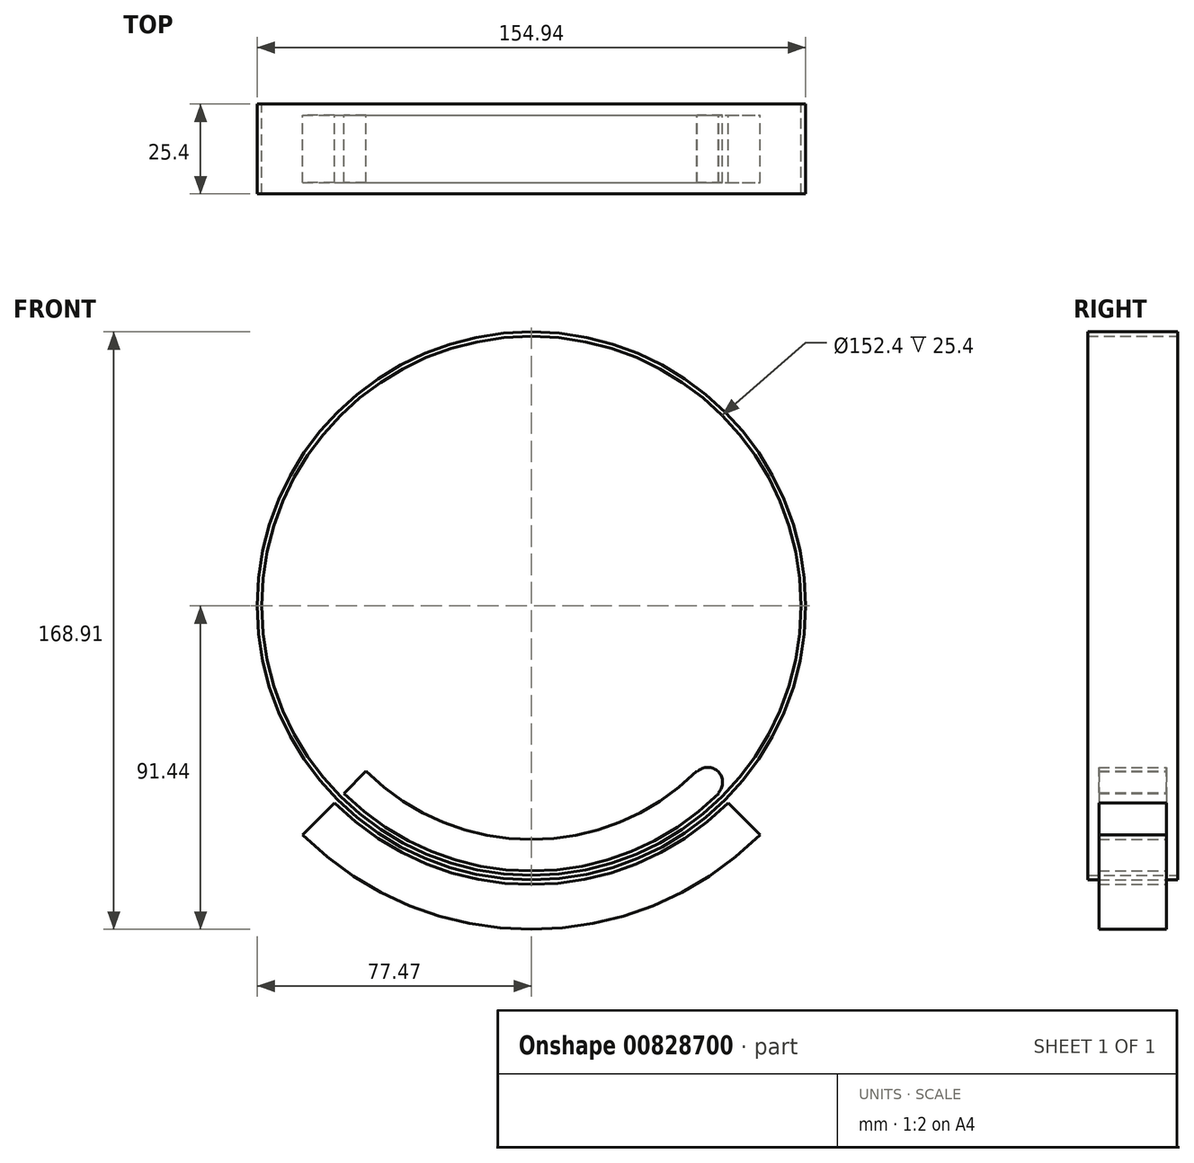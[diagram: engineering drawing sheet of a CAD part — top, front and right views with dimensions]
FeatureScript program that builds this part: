
annotation { "Feature Type Name" : "Feature", "Feature Type Description" : "" }
export const myFeature = defineFeature(function(context is Context, id is Id, definition is map)
    precondition{}
    {
        {
            var Q0;
            Q0=qCreatedBy(makeId("Front.planeOp"),FACE);
            var sketch = newSketch(context, id + "F0", { "sketchPlane" : qUnion([Q0])});
            skCircle(sketch, "E0", {"center": v(0, 0) * mm, "radius": 76.2 * mm});
            skCircle(sketch, "E1", {"center": v(0, 0) * mm, "radius": 77.47 * mm});
            skSolve(sketch);
        }
        {
            var Q0;
            Q0=qSketchRegion(id+"F0",true);
            extrude(context, id + "F1", {"entities" : qUnion([Q0]), "depth" : 25.4 * mm, "offsetDistance" : 25.4 * mm, "symmetric" : true});
        }
        {
            var Q0;
            Q0=qCreatedBy(makeId("Front.planeOp"),FACE);
            var sketch = newSketch(context, id + "F2", { "sketchPlane" : qUnion([Q0])});
            skLineSegment(sketch, "E2", {"start": v(-46.7, -46.7) * mm, "end": v(-52.98, -52.98) * mm});
            skLineSegment(sketch, "E3", {"start": v(46.7, -46.7) * mm, "end": v(46.88, -46.88) * mm});
            skArc(sketch, "E4", {"start": v(-52.98, -52.98) * mm, "mid": v(0, -74.93) * mm, "end": v(52.98, -52.98) * mm});
            skArc(sketch, "E5", {"start": v(-46.7, -46.7) * mm, "mid": v(0, -66.04) * mm, "end": v(46.7, -46.7) * mm});
            skArc(sketch, "E6", {"start": v(-55.68, -55.68) * mm, "mid": v(0, -78.74) * mm, "end": v(55.68, -55.68) * mm});
            skArc(sketch, "E7", {"start": v(-64.66, -64.66) * mm, "mid": v(0, -91.44) * mm, "end": v(64.66, -64.66) * mm});
            skLineSegment(sketch, "E8.trimOffspring", {"start": v(-55.68, -55.68) * mm, "end": v(-64.66, -64.66) * mm});
            skLineSegment(sketch, "E9.trimOffspring", {"start": v(55.68, -55.68) * mm, "end": v(64.66, -64.66) * mm});
            skArc(sketch, "E10", {"start": v(52.8, -52.8) * mm, "mid": v(52.8, -46.88) * mm, "end": v(46.88, -46.88) * mm});
            skLineSegment(sketch, "E11.trimOffspring", {"start": v(52.8, -52.8) * mm, "end": v(52.98, -52.98) * mm});
            skSolve(sketch);
        }
        {
            var Q0;
            Q0=qSketchRegion(id+"F2",true);
            extrude(context, id + "F3", {"entities" : qUnion([Q0]), "depth" : 19.05 * mm, "offsetDistance" : 25.4 * mm, "symmetric" : true});
        }
    });
